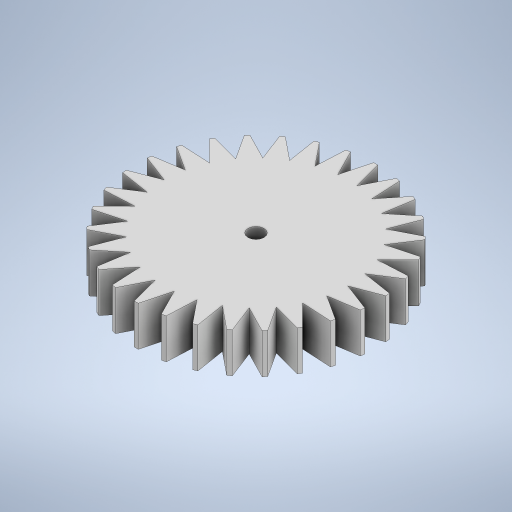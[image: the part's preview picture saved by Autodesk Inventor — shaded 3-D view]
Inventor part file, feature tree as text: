
AUTODESK INVENTOR PART (.ipt)
format: ipt  version: 2024 (Build 280153000, 153)  size: 352,768 bytes
history: native  units: mm
features: extrude x2, sketch x2
ambient origin geometry x8: Origin, YZ Plane, XZ Plane, XY Plane, X Axis, Y Axis, Z Axis, Center Point
bodies: Solid1 (feature_tree)
feature tree (4):
  extrude  "Extrusion1"  Depth=300.0mm TaperAngle=360.0deg
  extrude  "Extrusion4"  Depth=10.0mm TaperAngle=0.0deg
  sketch  "Sketch1"  dims[d0=30.0mm d1=300.0mm d3=360.0deg]
  sketch  "Sketch4"  dims[d5=5.0mm d6=0.0mm d15=10.0mm d16=0.0mm d17=2.0mm]
